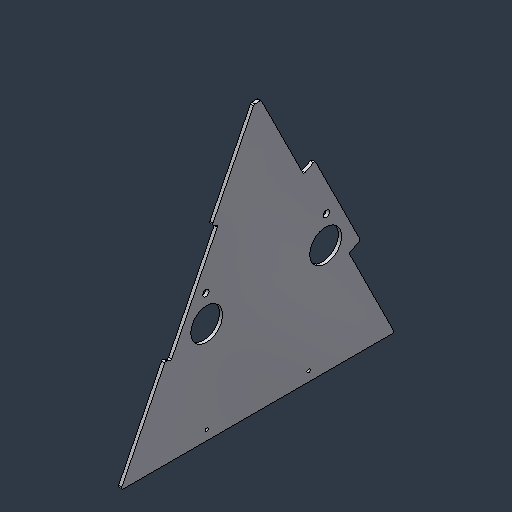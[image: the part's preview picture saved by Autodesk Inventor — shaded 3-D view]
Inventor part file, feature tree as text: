
AUTODESK INVENTOR PART (.ipt)
format: ipt  version: 2024.3 (Build 283343000, 343)  size: 107,520 bytes
history: native  units: mm (DEFAULTED — no unit token found)
features: fillet x1
ambient origin geometry x8: Origin, YZ Plane, XZ Plane, XY Plane, X Axis, Y Axis, Z Axis, Center Point
bodies: Solid1 (feature_tree)
feature tree (1):
  fillet  "Fillet1"  [1 undecoded]
note: 1 required parameter value undecoded (feature->parameter linkage not recoverable at this tier; creation-order binding heuristic only, values carry confidence <= 0.55)
